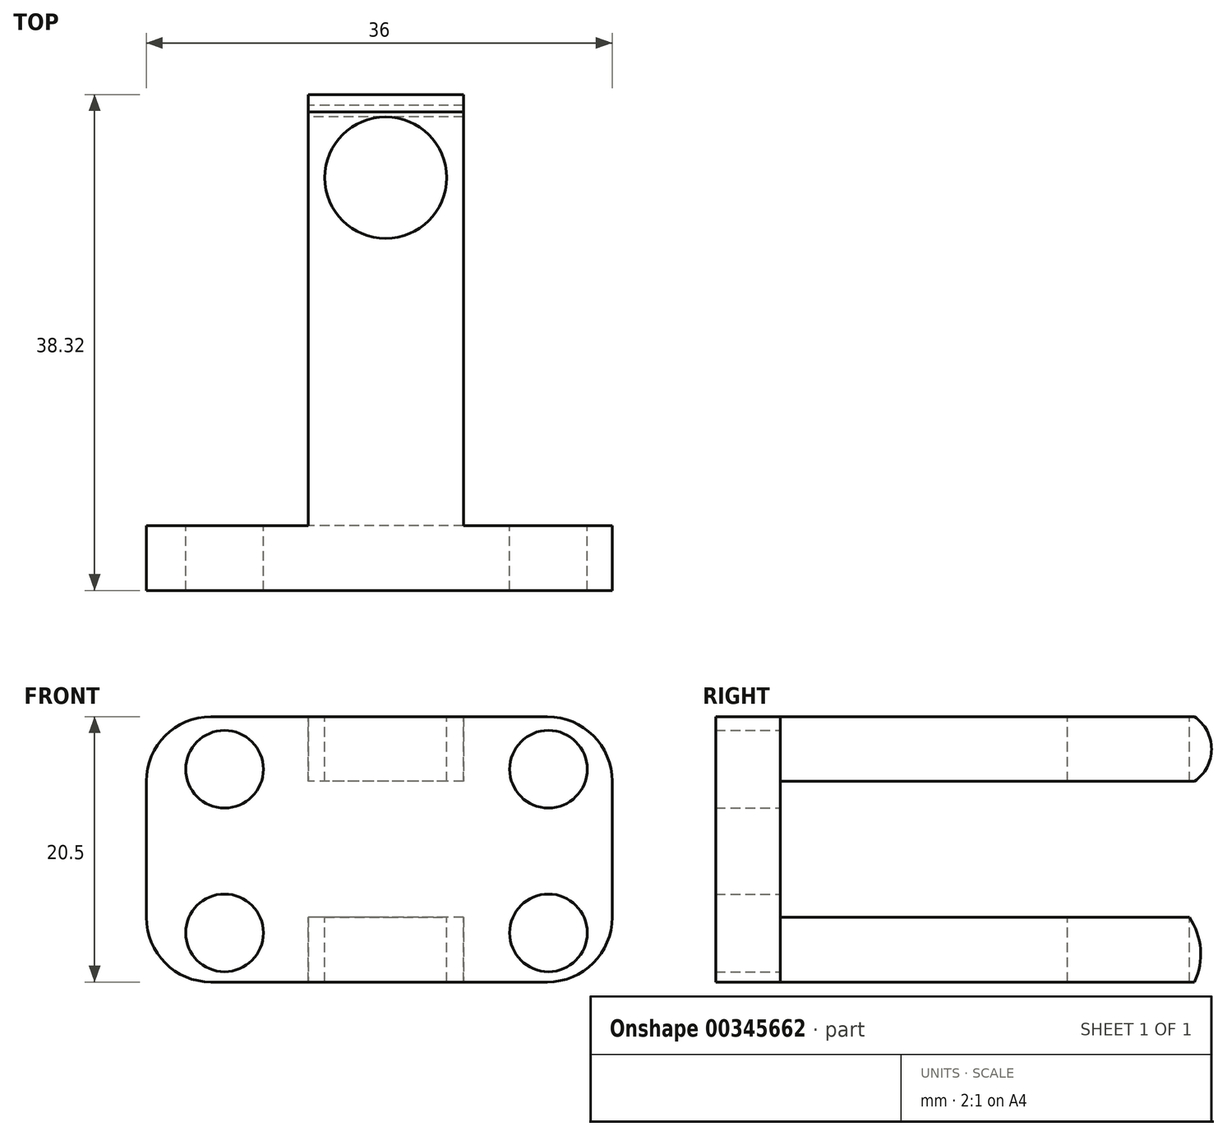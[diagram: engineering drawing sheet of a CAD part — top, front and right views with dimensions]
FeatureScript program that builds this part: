
annotation { "Feature Type Name" : "Feature", "Feature Type Description" : "" }
export const myFeature = defineFeature(function(context is Context, id is Id, definition is map)
    precondition{}
    {
        {
            var Q0;
            Q0=qCreatedBy(makeId("Front.planeOp"),FACE);
            var sketch = newSketch(context, id + "F0", { "sketchPlane" : qUnion([Q0])});
            skLineSegment(sketch, "E0", {"start": v(0, 0) * mm, "end": v(-13.5, 0) * mm});
            skLineSegment(sketch, "E1", {"start": v(-18.5, 5) * mm, "end": v(-18.5, 15.5) * mm});
            skLineSegment(sketch, "E2", {"start": v(-13.5, 20.5) * mm, "end": v(0, 20.5) * mm});
            skLineSegment(sketch, "E3.bottom", {"start": v(-13.5, 20.5) * mm, "end": v(12.5, 20.5) * mm});
            skLineSegment(sketch, "E3.top", {"start": v(-13.5, 0) * mm, "end": v(12.5, 0) * mm});
            skLineSegment(sketch, "E3.left", {"start": v(-18.5, 15.5) * mm, "end": v(-18.5, 5) * mm});
            skLineSegment(sketch, "E3.right", {"start": v(17.5, 15.5) * mm, "end": v(17.5, 5) * mm});
            skPoint(sketch, "E4.visualSharp", {"position": v(-18.5, 0) * mm});
            skPoint(sketch, "E5.visualSharp", {"position": v(-18.5, 20.5) * mm});
            skPoint(sketch, "E6.visualSharp", {"position": v(17.5, 20.5) * mm});
            skArc(sketch, "E6.filletArc", {"start": v(17.5, 15.5) * mm, "mid": v(16.04, 19.04) * mm, "end": v(12.5, 20.5) * mm});
            skPoint(sketch, "E7.visualSharp", {"position": v(17.5, 0) * mm});
            skArc(sketch, "E7.filletArc", {"start": v(12.5, 0) * mm, "mid": v(16.04, 1.46) * mm, "end": v(17.5, 5) * mm});
            skArc(sketch, "E8.filletArc", {"start": v(-18.5, 5) * mm, "mid": v(-17.04, 1.46) * mm, "end": v(-13.5, 0) * mm});
            skArc(sketch, "E9.filletArc", {"start": v(-13.5, 20.5) * mm, "mid": v(-17.04, 19.04) * mm, "end": v(-18.5, 15.5) * mm});
            skSolve(sketch);
        }
        {
            var Q0;
            Q0=qSketchRegion(id+"F0",true);
            var Q1;
            Q1=qSketchRegion(id+"F2",true);
            extrude(context, id + "F1", {"entities" : qUnion([Q0, Q1]), "depth" : 5 * mm});
        }
        {
            var Q0;
            Q0=qCreatedBy(makeId("Right.planeOp"),FACE);
            var sketch = newSketch(context, id + "F2", { "sketchPlane" : qUnion([Q0])});
            skLineSegment(sketch, "E10", {"start": v(0, 0) * mm, "end": v(32, 0) * mm});
            skLineSegment(sketch, "E11", {"start": v(0, 20.5) * mm, "end": v(32, 20.5) * mm});
            skLineSegment(sketch, "E12", {"start": v(22.88, 5) * mm, "end": v(0, 5) * mm});
            skLineSegment(sketch, "E13", {"start": v(31.6, 5) * mm, "end": v(22.88, 5) * mm});
            skLineSegment(sketch, "E14", {"start": v(0, 20.5) * mm, "end": v(0, 15.5) * mm});
            skLineSegment(sketch, "E15", {"start": v(0, 5) * mm, "end": v(0, 4.1) * mm});
            skLineSegment(sketch, "E16", {"start": v(0, 0) * mm, "end": v(0, 5) * mm});
            skArc(sketch, "E17", {"start": v(32, 0) * mm, "mid": v(32.47, 2.55) * mm, "end": v(31.6, 5) * mm});
            skLineSegment(sketch, "E18", {"start": v(0, 15.5) * mm, "end": v(32, 15.5) * mm});
            skArc(sketch, "E19", {"start": v(32, 15.5) * mm, "mid": v(33.32, 18) * mm, "end": v(32, 20.5) * mm});
            skSolve(sketch);
        }
        {
            var Q0;
            Q0=qSketchRegion(id+"F2",true);
            extrude(context, id + "F3", {"entities" : qUnion([Q0]), "operationType" : NewBodyOperationType.ADD, "depth" : 12 * mm, "symmetric" : true});
        }
        {
            var Q0;
            Q0=makeQuery(id+"F1.opExtrude","CAP_FACE",FACE,{"disambiguationData":[OSD([sQuery(id+"F0.wireOp",EDGE,"E3.bottom"),sQuery(id+"F0.wireOp",EDGE,"E3.top"),sQuery(id+"F0.wireOp",EDGE,"E3.left"),sQuery(id+"F0.wireOp",EDGE,"E3.right")])],"isStart":true});
            var sketch = newSketch(context, id + "F4", { "sketchPlane" : qUnion([Q0])});
            skLineSegment(sketch, "E20", {"start": v(0, 15.5) * mm, "end": v(0, 5) * mm});
            skCircle(sketch, "E21", {"center": v(12.45, 16.44) * mm, "radius": 3 * mm});
            skCircle(sketch, "E22", {"center": v(12.45, 3.8) * mm, "radius": 3 * mm});
            skCircle(sketch, "E23", {"center": v(-12.57, 16.44) * mm, "radius": 3 * mm});
            skCircle(sketch, "E24", {"center": v(-12.57, 3.8) * mm, "radius": 3 * mm});
            skPoint(sketch, "E25.center.orphan", {"position": v(0, 10.25) * mm});
            skSolve(sketch);
        }
        {
            var Q0;
            Q0=qSketchRegion(id+"F4",true);
            extrude(context, id + "F5", {"entities" : qUnion([Q0]), "operationType" : NewBodyOperationType.REMOVE, "oppositeDirection" : true, "depth" : 5 * mm});
        }
        {
            var Q0;
            Q0=makeQuery(id+"F3.boolean.opBoolean","MERGE",FACE,{"derivedFrom":[makeQuery(id+"F1.opExtrude","SWEPT_FACE",FACE,{"disambiguationData":[OSD([sQuery(id+"F0.wireOp",EDGE,"E3.bottom")])]}),makeQuery(id+"F3.opExtrude","SWEPT_FACE",FACE,{"disambiguationData":[OSD([sQuery(id+"F2.wireOp",EDGE,"E11")])]})]});
            var sketch = newSketch(context, id + "F6", { "sketchPlane" : qUnion([Q0])});
            skCircle(sketch, "E26", {"center": v(0, 26.9) * mm, "radius": 4.7 * mm});
            skPoint(sketch, "E27.orphan", {"position": v(0, 32) * mm});
            skSolve(sketch);
        }
        {
            var Q0;
            Q0=qSketchRegion(id+"F6",true);
            extrude(context, id + "F7", {"entities" : qUnion([Q0]), "operationType" : NewBodyOperationType.REMOVE, "oppositeDirection" : true, "depth" : 25 * mm});
        }
    });
